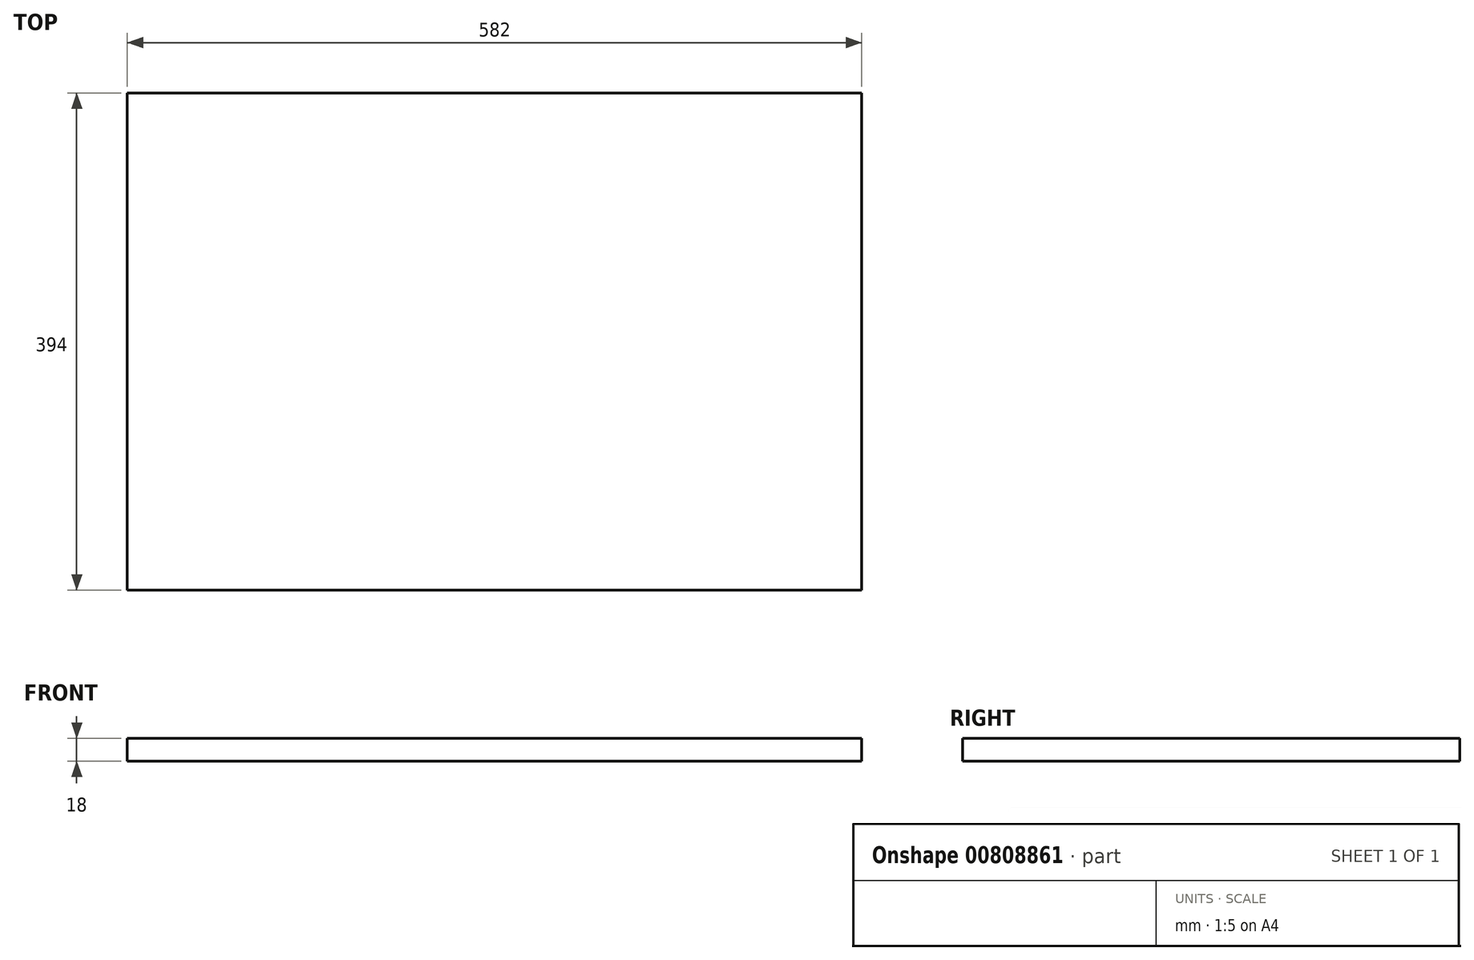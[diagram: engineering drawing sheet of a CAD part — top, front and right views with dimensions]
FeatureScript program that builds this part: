
annotation { "Feature Type Name" : "Feature", "Feature Type Description" : "" }
export const myFeature = defineFeature(function(context is Context, id is Id, definition is map)
    precondition{}
    {
        {
            var Q0;
            Q0=qCreatedBy(makeId("Top.planeOp"),FACE);
            var sketch = newSketch(context, id + "F0", { "sketchPlane" : qUnion([Q0])});
            skLineSegment(sketch, "E0.bottom", {"start": v(0, 0) * mm, "end": v(582, 0) * mm});
            skLineSegment(sketch, "E0.top", {"start": v(0, 394) * mm, "end": v(582, 394) * mm});
            skLineSegment(sketch, "E0.left", {"start": v(0, 0) * mm, "end": v(0, 394) * mm});
            skLineSegment(sketch, "E0.right", {"start": v(582, 0) * mm, "end": v(582, 394) * mm});
            skSolve(sketch);
        }
        {
            var Q0;
            Q0=makeQuery(id+"F0.imprint","IMPRINT",FACE,{"disambiguationData":[TD([[makeQuery(id+"F0.imprint","IMPRINT",EDGE,{"derivedFrom":sQuery(id+"F0.wireOp",EDGE,"E0.bottom")}),1.0]])]});
            extrude(context, id + "F1", {"entities" : qUnion([Q0]), "depth" : 18 * mm, "offsetDistance" : 25 * mm});
        }
    });
